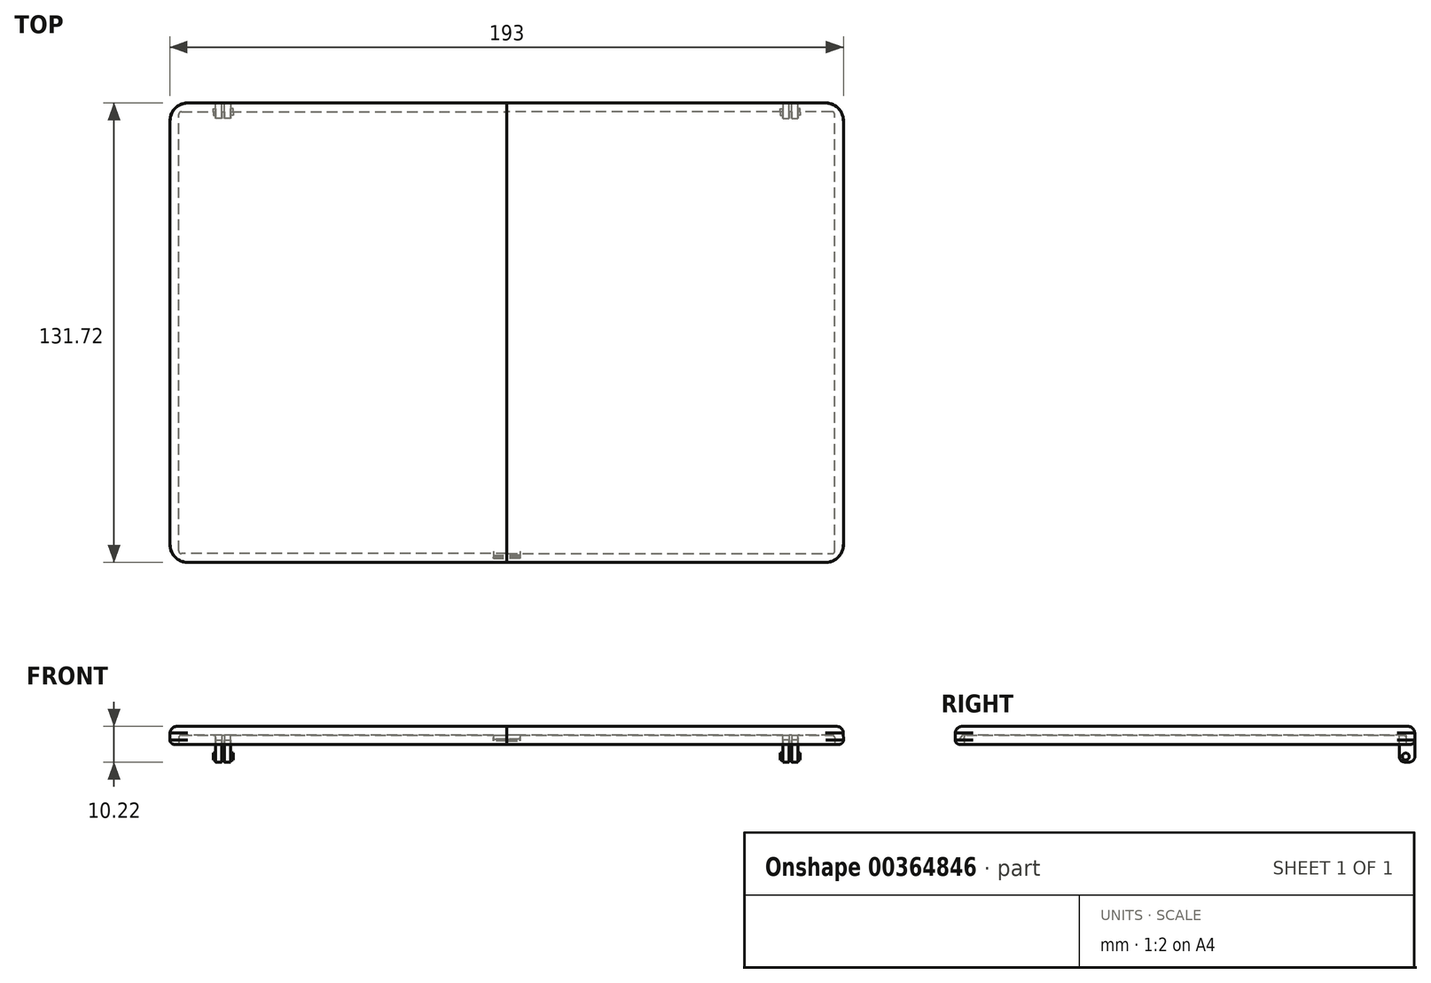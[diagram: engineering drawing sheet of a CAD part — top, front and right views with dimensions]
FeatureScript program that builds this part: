
annotation { "Feature Type Name" : "Feature", "Feature Type Description" : "" }
export const myFeature = defineFeature(function(context is Context, id is Id, definition is map)
    precondition{}
    {
        {
            var Q0;
            Q0=qCreatedBy(makeId("Top.planeOp"),FACE);
            var sketch = newSketch(context, id + "F0", { "sketchPlane" : qUnion([Q0])});
            skLineSegment(sketch, "E0.bottom", {"start": v(0, 65.88) * mm, "end": v(-96.52, 65.88) * mm});
            skLineSegment(sketch, "E0.top", {"start": v(0, -65.88) * mm, "end": v(-96.52, -65.88) * mm});
            skLineSegment(sketch, "E0.left", {"start": v(0, 65.88) * mm, "end": v(0, -65.88) * mm});
            skLineSegment(sketch, "E0.right", {"start": v(-96.52, 65.88) * mm, "end": v(-96.52, -65.88) * mm});
            skPoint(sketch, "E1", {"position": v(-96.52, 0) * mm});
            skLineSegment(sketch, "E2.bottom", {"start": v(0, 65.88) * mm, "end": v(96.52, 65.88) * mm});
            skLineSegment(sketch, "E2.top", {"start": v(0, -65.88) * mm, "end": v(96.52, -65.88) * mm});
            skLineSegment(sketch, "E2.right", {"start": v(96.52, 65.88) * mm, "end": v(96.52, -65.88) * mm});
            skSolve(sketch);
        }
        {
            var Q0;
            Q0=makeQuery(id+"F0.imprint","IMPRINT",FACE,{"disambiguationData":[TD([[makeQuery(id+"F0.imprint","IMPRINT",EDGE,{"derivedFrom":sQuery(id+"F0.wireOp",EDGE,"E0.bottom")}),1.0]])]});
            var Q1;
            Q1=makeQuery(id+"F0.imprint","IMPRINT",FACE,{"disambiguationData":[TD([[makeQuery(id+"F0.imprint","IMPRINT",EDGE,{"derivedFrom":sQuery(id+"F0.wireOp",EDGE,"E2.bottom")}),-1.0]])]});
            extrude(context, id + "F1", {"entities" : qUnion([Q0, Q1]), "depth" : 5.14 * mm, "hasDraft" : true, "draftAngle" : 1 * degree, "draftPullDirection" : true});
        }
        {
            var Q0;
            Q0=qCreatedBy(makeId("Top.planeOp"),FACE);
            var sketch = newSketch(context, id + "F2", { "sketchPlane" : qUnion([Q0])});
            skLineSegment(sketch, "E3.bottom", {"start": v(0, 72.75) * mm, "end": v(105.16, 72.75) * mm});
            skLineSegment(sketch, "E3.top", {"start": v(0, -72.07) * mm, "end": v(105.16, -72.07) * mm});
            skLineSegment(sketch, "E3.left", {"start": v(0, 72.75) * mm, "end": v(0, -72.07) * mm});
            skLineSegment(sketch, "E3.right", {"start": v(105.16, 72.75) * mm, "end": v(105.16, -72.07) * mm});
            skSolve(sketch);
        }
        {
            var Q0;
            Q0 = qSketchRegion(id + "F2", true);
            extrude(context, id + "F3", {"entities" : qUnion([Q0]), "operationType" : NewBodyOperationType.REMOVE, "depth" : 19.8 * mm});
        }
        {
            var Q0;
            Q0=makeQuery(id+"F1.opExtrude","SWEPT_EDGE",EDGE,{"disambiguationData":[OSD([sQuery(id+"F0.wireOp",EDGE,"E0.top"),sQuery(id+"F0.wireOp",EDGE,"E0.right")])]});
            var Q1;
            Q1=makeQuery(id+"F1.opExtrude","SWEPT_EDGE",EDGE,{"disambiguationData":[OSD([sQuery(id+"F0.wireOp",EDGE,"E0.bottom"),sQuery(id+"F0.wireOp",EDGE,"E0.right")])]});
            fillet(context, id + "F4", {"entities" : qUnion([Q0, Q1]), "radius" : 5.08 * mm, "tangentPropagation" : true, "allowEdgeOverflow" : false});
        }
        {
            var Q0;
            Q0=makeQuery(id+"F1.opExtrude","CAP_EDGE",EDGE,{"disambiguationData":[OSD([sQuery(id+"F0.wireOp",EDGE,"E0.top")])],"isStart":false});
            var Q1;
            {var subQ0=sQuery(id+"F0.wireOp",EDGE,"E0.right");var subQ1=sQuery(id+"F0.wireOp",EDGE,"E0.top");Q1=makeQuery(id+"F4.opFillet","BLEND_EDGE",EDGE,{"blendedFrom":[makeQuery(id+"F1.opExtrude","SWEPT_EDGE",EDGE,{"disambiguationData":[OSD([subQ1,subQ0])]}),makeQuery(id+"F1.opExtrude","CAP_FACE",FACE,{"disambiguationData":[OSD([sQuery(id+"F0.wireOp",EDGE,"E0.bottom"),subQ1,sQuery(id+"F0.wireOp",EDGE,"E0.left"),subQ0])],"isStart":false})],"blendedInto":[makeQuery(id+"F1.opExtrude","CAP_FACE",FACE,{"disambiguationData":[OSD([sQuery(id+"F0.wireOp",EDGE,"E0.bottom"),subQ1,sQuery(id+"F0.wireOp",EDGE,"E0.left"),subQ0])],"isStart":false})]});}
            var Q2;
            Q2=makeQuery(id+"F1.opExtrude","CAP_EDGE",EDGE,{"disambiguationData":[OSD([sQuery(id+"F0.wireOp",EDGE,"E0.right")])],"isStart":false});
            var Q3;
            {var subQ0=sQuery(id+"F0.wireOp",EDGE,"E0.right");var subQ1=sQuery(id+"F0.wireOp",EDGE,"E0.bottom");Q3=makeQuery(id+"F4.opFillet","BLEND_EDGE",EDGE,{"blendedFrom":[makeQuery(id+"F1.opExtrude","SWEPT_EDGE",EDGE,{"disambiguationData":[OSD([subQ1,subQ0])]}),makeQuery(id+"F1.opExtrude","CAP_FACE",FACE,{"disambiguationData":[OSD([subQ1,sQuery(id+"F0.wireOp",EDGE,"E0.top"),sQuery(id+"F0.wireOp",EDGE,"E0.left"),subQ0])],"isStart":false})],"blendedInto":[makeQuery(id+"F1.opExtrude","CAP_FACE",FACE,{"disambiguationData":[OSD([subQ1,sQuery(id+"F0.wireOp",EDGE,"E0.top"),sQuery(id+"F0.wireOp",EDGE,"E0.left"),subQ0])],"isStart":false})]});}
            var Q4;
            Q4=makeQuery(id+"F1.opExtrude","CAP_EDGE",EDGE,{"disambiguationData":[OSD([sQuery(id+"F0.wireOp",EDGE,"E0.bottom")])],"isStart":false});
            fillet(context, id + "F5", {"entities" : qUnion([Q0, Q1, Q2, Q3, Q4]), "radius" : 1.9 * mm, "tangentPropagation" : true, "allowEdgeOverflow" : false});
        }
        {
            var Q0;
            Q0=makeQuery(id+"F1.opExtrude","CAP_EDGE",EDGE,{"disambiguationData":[OSD([sQuery(id+"F0.wireOp",EDGE,"E0.right")])],"isStart":true});
            fillet(context, id + "F6", {"entities" : qUnion([Q0]), "radius" : 1.27 * mm, "tangentPropagation" : true, "allowEdgeOverflow" : false});
        }
        {
            var Q0;
            Q0=qCreatedBy(makeId("Top.planeOp"),FACE);
            var sketch = newSketch(context, id + "F7", { "sketchPlane" : qUnion([Q0])});
            skLineSegment(sketch, "E4.bottom", {"start": v(0, -63.34) * mm, "end": v(-93.22, -63.34) * mm});
            skLineSegment(sketch, "E4.left", {"start": v(0, -63.34) * mm, "end": v(0, 63.34) * mm});
            skLineSegment(sketch, "E4.right", {"start": v(-93.98, -62.58) * mm, "end": v(-93.98, 62.58) * mm});
            skPoint(sketch, "E5.visualSharp", {"position": v(-93.98, -63.34) * mm});
            skArc(sketch, "E5.filletArc", {"start": v(-93.22, -63.34) * mm, "mid": v(-93.76, -63.12) * mm, "end": v(-93.98, -62.58) * mm});
            skLineSegment(sketch, "E6", {"start": v(-93.22, 63.34) * mm, "end": v(0, 63.34) * mm});
            skPoint(sketch, "E7.visualSharp", {"position": v(-93.98, 63.34) * mm});
            skArc(sketch, "E7.filletArc", {"start": v(-93.22, 63.34) * mm, "mid": v(-93.76, 63.12) * mm, "end": v(-93.98, 62.58) * mm});
            skLineSegment(sketch, "E8.bottom", {"start": v(0, 63.34) * mm, "end": v(5.47, 63.34) * mm});
            skLineSegment(sketch, "E8.top", {"start": v(0, -63.34) * mm, "end": v(5.47, -63.34) * mm});
            skLineSegment(sketch, "E8.left", {"start": v(0, 63.34) * mm, "end": v(0, -63.34) * mm});
            skLineSegment(sketch, "E8.right", {"start": v(5.47, 63.34) * mm, "end": v(5.47, -63.34) * mm});
            skSolve(sketch);
        }
        {
            var Q0;
            Q0=makeQuery(id+"F7.imprint","IMPRINT",FACE,{"disambiguationData":[TD([[makeQuery(id+"F7.imprint","IMPRINT",EDGE,{"derivedFrom":sQuery(id+"F7.wireOp",EDGE,"E4.bottom")}),1.0]])]});
            var Q1;
            Q1=makeQuery(id+"F7.imprint","IMPRINT",FACE,{"disambiguationData":[TD([[makeQuery(id+"F7.imprint","IMPRINT",EDGE,{"derivedFrom":sQuery(id+"F7.wireOp",EDGE,"E4.bottom")}),-1.0]])]});
            var Q2;
            Q2=makeQuery(id+"F7.imprint","IMPRINT",FACE,{"disambiguationData":[TD([[makeQuery(id+"F7.imprint","IMPRINT",EDGE,{"derivedFrom":sQuery(id+"F7.wireOp",EDGE,"E8.bottom")}),-1.0]])]});
            extrude(context, id + "F8", {"entities" : qUnion([Q0, Q1, Q2]), "operationType" : NewBodyOperationType.REMOVE, "depth" : 2.6 * mm, "hasDraft" : true, "draftAngle" : 1 * degree, "draftPullDirection" : true});
        }
        {
            var Q0;
            Q0=qCreatedBy(makeId("Top.planeOp"),FACE);
            var sketch = newSketch(context, id + "F9", { "sketchPlane" : qUnion([Q0])});
            skLineSegment(sketch, "E9.bottom", {"start": v(-83.44, 65.86) * mm, "end": v(-81.66, 65.86) * mm});
            skLineSegment(sketch, "E9.top", {"start": v(-83.44, 61.41) * mm, "end": v(-81.66, 61.41) * mm});
            skLineSegment(sketch, "E9.left", {"start": v(-83.44, 61.41) * mm, "end": v(-83.44, 65.86) * mm});
            skLineSegment(sketch, "E9.right", {"start": v(-81.66, 61.41) * mm, "end": v(-81.66, 65.86) * mm});
            skLineSegment(sketch, "E10.top", {"start": v(-80.9, 61.41) * mm, "end": v(-79.12, 61.41) * mm});
            skLineSegment(sketch, "E10.left", {"start": v(-80.9, 61.41) * mm, "end": v(-80.9, 65.86) * mm});
            skLineSegment(sketch, "E10.right", {"start": v(-79.12, 65.86) * mm, "end": v(-79.12, 61.41) * mm});
            skLineSegment(sketch, "E11", {"start": v(-83.44, 63.64) * mm, "end": v(-79.12, 63.64) * mm, "construction": true});
            skPoint(sketch, "E12", {"position": v(-81.28, 63.64) * mm});
            skLineSegment(sketch, "E13", {"start": v(-80.9, 65.86) * mm, "end": v(-79.12, 65.86) * mm});
            skPoint(sketch, "E14.orphan", {"position": v(-79.12, 65.86) * mm});
            skSolve(sketch);
        }
        {
            var Q0;
            Q0=makeQuery(id+"F9.imprint","IMPRINT",FACE,{"disambiguationData":[TD([[makeQuery(id+"F9.imprint","IMPRINT",EDGE,{"derivedFrom":sQuery(id+"F9.wireOp",EDGE,"E9.bottom")}),-1.0]])]});
            var Q1;
            Q1=makeQuery(id+"F9.imprint","IMPRINT",FACE,{"disambiguationData":[TD([[makeQuery(id+"F9.imprint","IMPRINT",EDGE,{"derivedFrom":sQuery(id+"F9.wireOp",EDGE,"E10.top")}),1.0]])]});
            extrude(context, id + "F10", {"entities" : qUnion([Q0, Q1]), "operationType" : NewBodyOperationType.ADD, "oppositeDirection" : true, "depth" : 5.08 * mm, "hasSecondDirection" : true, "secondDirectionOppositeDirection" : false, "secondDirectionDepth" : 1.35 * mm});
        }
        {
            var Q0;
            Q0=makeQuery(id+"F10.opExtrude","CAP_FACE",FACE,{"disambiguationData":[OSD([sQuery(id+"F9.wireOp",EDGE,"E9.bottom"),sQuery(id+"F9.wireOp",EDGE,"E9.top"),sQuery(id+"F9.wireOp",EDGE,"E9.left"),sQuery(id+"F9.wireOp",EDGE,"E9.right")])],"isStart":true});
            var Q1;
            Q1=makeQuery(id+"F10.opExtrude","CAP_FACE",FACE,{"disambiguationData":[OSD([sQuery(id+"F9.wireOp",EDGE,"E10.top"),sQuery(id+"F9.wireOp",EDGE,"E10.left"),sQuery(id+"F9.wireOp",EDGE,"E10.right"),sQuery(id+"F9.wireOp",EDGE,"E13")])],"isStart":true});
            extrude(context, id + "F11", {"entities" : qUnion([Q0, Q1]), "operationType" : NewBodyOperationType.ADD, "depth" : 1.45 * mm});
        }
        {
            var Q0;
            Q0=qCreatedBy(makeId("Right.planeOp"),FACE);
            var sketch = newSketch(context, id + "F12", { "sketchPlane" : qUnion([Q0])});
            skLineSegment(sketch, "E15.bottom", {"start": v(-63.2, 2.6) * mm, "end": v(-64.66, 2.6) * mm});
            skLineSegment(sketch, "E15.top", {"start": v(-63.2, 0.93) * mm, "end": v(-64.66, 0.93) * mm});
            skLineSegment(sketch, "E15.left", {"start": v(-63.2, 2.6) * mm, "end": v(-63.2, 0.93) * mm});
            skLineSegment(sketch, "E15.right", {"start": v(-64.66, 2.6) * mm, "end": v(-64.66, 0.93) * mm});
            skLineSegment(sketch, "E16", {"start": v(-63.8, 2.6) * mm, "end": v(-64.66, 1.55) * mm});
            skLineSegment(sketch, "E17.bottom", {"start": v(-63.2, 0.93) * mm, "end": v(-63.64, 0.93) * mm});
            skLineSegment(sketch, "E17.top", {"start": v(-63.2, 0) * mm, "end": v(-63.64, 0) * mm});
            skLineSegment(sketch, "E17.left", {"start": v(-63.2, 0.93) * mm, "end": v(-63.2, 0) * mm});
            skLineSegment(sketch, "E17.right", {"start": v(-63.64, 0.93) * mm, "end": v(-63.64, 0) * mm});
            skSolve(sketch);
        }
        {
            var Q0;
            {var subQ1=sQuery(id+"F12.wireOp",EDGE,"E15.top");Q0=makeQuery(id+"F12.imprint","IMPRINT",FACE,{"disambiguationData":[TD([[makeQuery(id+"F12.imprint","IMPRINT",EDGE,{"derivedFrom":subQ1}),-1.0]])]});}
            var Q1;
            Q1=makeQuery(id+"F12.imprint","IMPRINT",FACE,{"disambiguationData":[TD([[makeQuery(id+"F12.imprint","IMPRINT",EDGE,{"derivedFrom":sQuery(id+"F12.wireOp",EDGE,"E17.bottom")}),1.0]])]});
            extrude(context, id + "F13", {"entities" : qUnion([Q0, Q1]), "operationType" : NewBodyOperationType.REMOVE, "oppositeDirection" : true, "depth" : 3.8 * mm});
        }
        {
            var Q0;
            Q0=makeQuery(id+"F10.opExtrude","CAP_EDGE",EDGE,{"disambiguationData":[OSD([sQuery(id+"F9.wireOp",EDGE,"E9.bottom")])],"isStart":false});
            var Q1;
            Q1=makeQuery(id+"F10.opExtrude","CAP_EDGE",EDGE,{"disambiguationData":[OSD([sQuery(id+"F9.wireOp",EDGE,"E13")])],"isStart":false});
            var Q2;
            Q2=makeQuery(id+"F10.opExtrude","CAP_EDGE",EDGE,{"disambiguationData":[OSD([sQuery(id+"F9.wireOp",EDGE,"E10.top")])],"isStart":false});
            var Q3;
            Q3=makeQuery(id+"F10.opExtrude","CAP_EDGE",EDGE,{"disambiguationData":[OSD([sQuery(id+"F9.wireOp",EDGE,"E9.top")])],"isStart":false});
            fillet(context, id + "F14", {"entities" : qUnion([Q0, Q1, Q2, Q3]), "radius" : 1.59 * mm, "tangentPropagation" : true, "allowEdgeOverflow" : false});
        }
        {
            var Q0;
            {var subQ0=sQuery(id+"F9.wireOp",EDGE,"E9.left");Q0=makeQuery(id+"FubJW8Bf5jqRAiZ_1.boolean.opBoolean","MERGE",FACE,{"derivedFrom":[makeQuery(id+"F10.opExtrude","SWEPT_FACE",FACE,{"disambiguationData":[OSD([subQ0])]}),makeQuery(id+"FubJW8Bf5jqRAiZ_1.opExtrude","SWEPT_FACE",FACE,{"disambiguationData":[OSD([subQ0])]})]});}
            var sketch = newSketch(context, id + "F15", { "sketchPlane" : qUnion([Q0])});
            skCircle(sketch, "E18", {"center": v(-63.26, -3.5) * mm, "radius": 1 * mm});
            skSolve(sketch);
        }
        {
            var Q0;
            Q0 = qSketchRegion(id + "F15", true);
            extrude(context, id + "F16", {"entities" : qUnion([Q0]), "operationType" : NewBodyOperationType.ADD, "depth" : 0.66 * mm});
        }
        {
            var Q0;
            {var subQ0=sQuery(id+"F9.wireOp",EDGE,"E10.right");Q0=makeQuery(id+"FubJW8Bf5jqRAiZ_1.boolean.opBoolean","MERGE",FACE,{"derivedFrom":[makeQuery(id+"F10.opExtrude","SWEPT_FACE",FACE,{"disambiguationData":[OSD([subQ0])]}),makeQuery(id+"FubJW8Bf5jqRAiZ_1.opExtrude","SWEPT_FACE",FACE,{"disambiguationData":[OSD([subQ0])]})]});}
            var sketch = newSketch(context, id + "F17", { "sketchPlane" : qUnion([Q0])});
            skCircle(sketch, "E19", {"center": v(63.26, -3.5) * mm, "radius": 1 * mm});
            skSolve(sketch);
        }
        {
            var Q0;
            Q0=makeQuery(id+"F17.imprint","IMPRINT",FACE,{"disambiguationData":[TD([[makeQuery(id+"F17.imprint","IMPRINT",EDGE,{"derivedFrom":sQuery(id+"F17.wireOp",EDGE,"E19")}),1.0]])]});
            extrude(context, id + "F18", {"entities" : qUnion([Q0]), "operationType" : NewBodyOperationType.ADD, "depth" : 0.76 * mm});
        }
        {
            var Q0;
            Q0=makeQuery(id+"F13.boolean.opBoolean","COPY",EDGE,{"derivedFrom":makeQuery(id+"F13.opExtrude","SWEPT_EDGE",EDGE,{"disambiguationData":[OSD([sQuery(id+"F12.wireOp",EDGE,"E15.top"),sQuery(id+"F12.wireOp",EDGE,"E17.bottom"),sQuery(id+"F12.wireOp",EDGE,"E17.right")])]})});
            chamfer(context, id + "F19", {"entities" : qUnion([Q0]), "chamferType" : ChamferType.OFFSET_ANGLE, "width" : 0.5 * mm, "oppositeDirection" : true, "angle" : 30 * degree, "tangentPropagation" : true});
        }
        {
            var Q0;
            Q0=makeQuery(id+"F8.boolean.opBoolean","COPY",EDGE,{"derivedFrom":makeQuery(id+"F8.opExtrude","CAP_EDGE",EDGE,{"disambiguationData":[OSD([sQuery(id+"F7.wireOp",EDGE,"E4.bottom")])],"isStart":false})});
            fillet(context, id + "F20", {"entities" : qUnion([Q0]), "radius" : 0.64 * mm, "tangentPropagation" : true, "allowEdgeOverflow" : false});
        }
        {
            var Q0;
            {var subQ0=sQuery(id+"F0.wireOp",EDGE,"E2.right");var subQ1=sQuery(id+"F0.wireOp",EDGE,"E2.top");var subQ2=sQuery(id+"F0.wireOp",EDGE,"E2.bottom");var subQ3=sQuery(id+"F0.wireOp",EDGE,"E0.right");var subQ4=sQuery(id+"F0.wireOp",EDGE,"E0.top");var subQ5=sQuery(id+"F0.wireOp",EDGE,"E0.bottom");Q0=makeQuery(id+"F5.opFillet","BLEND_FACE",FACE,{"disambiguationData":[OSD([subQ5,subQ4,subQ3,subQ2,subQ1,subQ0]),TDD([makeQuery(id+"F4.opFillet","BLEND_EDGE",EDGE,{"blendedFrom":[makeQuery(id+"F1.opExtrude","SWEPT_EDGE",EDGE,{"disambiguationData":[OSD([subQ4,subQ3])]}),makeQuery(id+"F1.opExtrude","CAP_FACE",FACE,{"disambiguationData":[OSD([subQ5,subQ4,subQ3,subQ2,subQ1,subQ0])],"isStart":false})],"blendedInto":[makeQuery(id+"F1.opExtrude","CAP_FACE",FACE,{"disambiguationData":[OSD([subQ5,subQ4,subQ3,subQ2,subQ1,subQ0])],"isStart":false})]})])]});}
            var Q1;
            Q1=makeQuery(id+"F5.opFillet","BLEND_FACE",FACE,{"disambiguationData":[OSD([sQuery(id+"F0.wireOp",EDGE,"E0.right")])]});
            var Q2;
            Q2=makeQuery(id+"F5.opFillet","BLEND_FACE",FACE,{"disambiguationData":[OSD([sQuery(id+"F0.wireOp",EDGE,"E0.bottom"),sQuery(id+"F0.wireOp",EDGE,"E2.bottom")])]});
            var Q3;
            Q3=makeQuery(id+"F5.opFillet","BLEND_FACE",FACE,{"disambiguationData":[OSD([sQuery(id+"F0.wireOp",EDGE,"E0.top"),sQuery(id+"F0.wireOp",EDGE,"E2.top")])]});
            var Q4;
            Q4=makeQuery(id+"F1.opExtrude","CAP_FACE",FACE,{"disambiguationData":[OSD([sQuery(id+"F0.wireOp",EDGE,"E0.bottom"),sQuery(id+"F0.wireOp",EDGE,"E0.top"),sQuery(id+"F0.wireOp",EDGE,"E0.right"),sQuery(id+"F0.wireOp",EDGE,"E2.bottom"),sQuery(id+"F0.wireOp",EDGE,"E2.top"),sQuery(id+"F0.wireOp",EDGE,"E2.right")])],"isStart":false});
            var Q5;
            Q5=makeQuery(id+"F6.opFillet","BLEND_FACE",FACE,{"disambiguationData":[OSD([sQuery(id+"F0.wireOp",EDGE,"E0.top"),sQuery(id+"F0.wireOp",EDGE,"E2.top")])]});
            var Q6;
            Q6=makeQuery(id+"F1.opExtrude","SWEPT_FACE",FACE,{"disambiguationData":[OSD([sQuery(id+"F0.wireOp",EDGE,"E0.top"),sQuery(id+"F0.wireOp",EDGE,"E2.top")])]});
            var Q7;
            {var subQ0=sQuery(id+"F7.wireOp",EDGE,"E8.bottom");var subQ1=sQuery(id+"F7.wireOp",EDGE,"E6");Q7=makeQuery(id+"F11.boolean.opBoolean","SPLIT",FACE,{"disambiguationData":[TD([makeQuery(id+"F3.boolean.opBoolean","COPY",FACE,{"derivedFrom":makeQuery(id+"F3.opExtrude","SWEPT_FACE",FACE,{"disambiguationData":[OSD([sQuery(id+"F2.wireOp",EDGE,"E3.left")])]})})])],"derivedFrom":makeQuery(id+"F8.boolean.opBoolean","COPY",FACE,{"derivedFrom":makeQuery(id+"F8.opExtrude","SWEPT_FACE",FACE,{"disambiguationData":[OSD([subQ1,subQ0])]})})});}
            var Q8;
            Q8=makeQuery(id+"F13.boolean.opBoolean","MERGE",FACE,{"derivedFrom":[makeQuery(id+"F8.boolean.opBoolean","COPY",FACE,{"derivedFrom":makeQuery(id+"F8.opExtrude","CAP_FACE",FACE,{"disambiguationData":[OSD([sQuery(id+"F7.wireOp",EDGE,"E4.bottom"),sQuery(id+"F7.wireOp",EDGE,"E4.right"),sQuery(id+"F7.wireOp",EDGE,"E5.filletArc"),sQuery(id+"F7.wireOp",EDGE,"E6"),sQuery(id+"F7.wireOp",EDGE,"E7.filletArc"),sQuery(id+"F7.wireOp",EDGE,"E8.bottom"),sQuery(id+"F7.wireOp",EDGE,"E8.top"),sQuery(id+"F7.wireOp",EDGE,"E8.right")])],"isStart":false})}),makeQuery(id+"F13.opExtrude","SWEPT_FACE",FACE,{"disambiguationData":[OSD([sQuery(id+"F12.wireOp",EDGE,"E15.bottom")])]})]});
            var Q9;
            Q9=makeQuery(id+"F3.boolean.opBoolean","COPY",FACE,{"derivedFrom":makeQuery(id+"F3.opExtrude","SWEPT_FACE",FACE,{"disambiguationData":[OSD([sQuery(id+"F2.wireOp",EDGE,"E3.left")])]})});
            var Q10;
            Q10=makeQuery(id+"F20.opFillet","BLEND_FACE",FACE,{"disambiguationData":[OSD([sQuery(id+"F7.wireOp",EDGE,"E7.filletArc")])]});
            var Q11;
            {var subQ0=sQuery(id+"F0.wireOp",EDGE,"E2.right");var subQ1=sQuery(id+"F0.wireOp",EDGE,"E2.top");var subQ2=sQuery(id+"F0.wireOp",EDGE,"E2.bottom");var subQ3=sQuery(id+"F0.wireOp",EDGE,"E0.right");var subQ4=sQuery(id+"F0.wireOp",EDGE,"E0.top");var subQ5=sQuery(id+"F0.wireOp",EDGE,"E0.bottom");Q11=makeQuery(id+"F5.opFillet","BLEND_FACE",FACE,{"disambiguationData":[OSD([subQ5,subQ4,subQ3,subQ2,subQ1,subQ0]),TDD([makeQuery(id+"F4.opFillet","BLEND_EDGE",EDGE,{"blendedFrom":[makeQuery(id+"F1.opExtrude","SWEPT_EDGE",EDGE,{"disambiguationData":[OSD([subQ5,subQ3])]}),makeQuery(id+"F1.opExtrude","CAP_FACE",FACE,{"disambiguationData":[OSD([subQ5,subQ4,subQ3,subQ2,subQ1,subQ0])],"isStart":false})],"blendedInto":[makeQuery(id+"F1.opExtrude","CAP_FACE",FACE,{"disambiguationData":[OSD([subQ5,subQ4,subQ3,subQ2,subQ1,subQ0])],"isStart":false})]})])]});}
            var Q12;
            {var subQ0=sQuery(id+"F0.wireOp",EDGE,"E2.right");var subQ1=sQuery(id+"F0.wireOp",EDGE,"E2.top");var subQ2=sQuery(id+"F0.wireOp",EDGE,"E2.bottom");var subQ3=sQuery(id+"F0.wireOp",EDGE,"E0.right");var subQ4=sQuery(id+"F0.wireOp",EDGE,"E0.top");var subQ5=sQuery(id+"F0.wireOp",EDGE,"E0.bottom");Q12=makeQuery(id+"F6.opFillet","BLEND_FACE",FACE,{"disambiguationData":[OSD([subQ5,subQ4,subQ3,subQ2,subQ1,subQ0]),TDD([makeQuery(id+"F4.opFillet","BLEND_EDGE",EDGE,{"blendedFrom":[makeQuery(id+"F1.opExtrude","SWEPT_EDGE",EDGE,{"disambiguationData":[OSD([subQ4,subQ3])]}),makeQuery(id+"F1.opExtrude","CAP_FACE",FACE,{"disambiguationData":[OSD([subQ5,subQ4,subQ3,subQ2,subQ1,subQ0])],"isStart":true})],"blendedInto":[makeQuery(id+"F1.opExtrude","CAP_FACE",FACE,{"disambiguationData":[OSD([subQ5,subQ4,subQ3,subQ2,subQ1,subQ0])],"isStart":true})]})])]});}
            var Q13;
            Q13=makeQuery(id+"F1.opExtrude","SWEPT_FACE",FACE,{"disambiguationData":[OSD([sQuery(id+"F0.wireOp",EDGE,"E0.right")])]});
            var Q14;
            Q14=makeQuery(id+"F14.opFillet","BLEND_FACE",FACE,{"disambiguationData":[OSD([sQuery(id+"F9.wireOp",EDGE,"E10.top")])]});
            var Q15;
            Q15=makeQuery(id+"F20.opFillet","BLEND_FACE",FACE,{"disambiguationData":[OSD([sQuery(id+"F7.wireOp",EDGE,"E4.bottom"),sQuery(id+"F7.wireOp",EDGE,"E8.top")])]});
            var Q16;
            Q16=makeQuery(id+"F8.boolean.opBoolean","COPY",FACE,{"derivedFrom":makeQuery(id+"F8.opExtrude","SWEPT_FACE",FACE,{"disambiguationData":[OSD([sQuery(id+"F7.wireOp",EDGE,"E4.right")])]})});
            var Q17;
            Q17=makeQuery(id+"F1.opExtrude","SWEPT_FACE",FACE,{"disambiguationData":[OSD([sQuery(id+"F0.wireOp",EDGE,"E0.bottom"),sQuery(id+"F0.wireOp",EDGE,"E2.bottom")])]});
            var Q18;
            {var subQ0=sQuery(id+"F0.wireOp",EDGE,"E2.top");var subQ1=sQuery(id+"F0.wireOp",EDGE,"E0.top");var subQ2=sQuery(id+"F0.wireOp",EDGE,"E2.bottom");var subQ3=sQuery(id+"F0.wireOp",EDGE,"E0.bottom");var subQ4=sQuery(id+"F0.wireOp",EDGE,"E0.right");var subQ5=sQuery(id+"F0.wireOp",EDGE,"E2.right");var subQ6=makeQuery(id+"F1.opExtrude","CAP_FACE",FACE,{"disambiguationData":[OSD([subQ3,subQ1,subQ4,subQ2,subQ0,subQ5])],"isStart":true});Q18=makeQuery(id+"F10.boolean.opBoolean","SPLIT",FACE,{"disambiguationData":[TD([makeQuery(id+"F6.opFillet","BLEND_FACE",FACE,{"disambiguationData":[OSD([subQ4])]})])],"derivedFrom":subQ6});}
            var Q19;
            Q19=makeQuery(id+"F20.opFillet","BLEND_FACE",FACE,{"disambiguationData":[OSD([sQuery(id+"F7.wireOp",EDGE,"E4.right")])]});
            var Q20;
            {var subQ0=sQuery(id+"F9.wireOp",EDGE,"E10.top");Q20=makeQuery(id+"F11.boolean.opBoolean","MERGE",FACE,{"derivedFrom":[makeQuery(id+"F10.opExtrude","SWEPT_FACE",FACE,{"disambiguationData":[OSD([subQ0])]}),makeQuery(id+"F11.opExtrude","SWEPT_FACE",FACE,{"disambiguationData":[OSD([subQ0])]})]});}
            var Q21;
            Q21=makeQuery(id+"F18.opExtrude","SWEPT_FACE",FACE,{"disambiguationData":[OSD([sQuery(id+"F17.wireOp",EDGE,"E19")])]});
            var Q22;
            {var subQ0=sQuery(id+"F0.wireOp",EDGE,"E2.bottom");var subQ1=sQuery(id+"F0.wireOp",EDGE,"E0.bottom");Q22=makeQuery(id+"F10.boolean.opBoolean","SPLIT",FACE,{"disambiguationData":[TD([makeQuery(id+"F10.opExtrude","SWEPT_FACE",FACE,{"disambiguationData":[OSD([sQuery(id+"F9.wireOp",EDGE,"E10.right")])]})])],"derivedFrom":makeQuery(id+"F1.opExtrude","CAP_FACE",FACE,{"disambiguationData":[OSD([subQ1,sQuery(id+"F0.wireOp",EDGE,"E0.top"),sQuery(id+"F0.wireOp",EDGE,"E0.right"),subQ0,sQuery(id+"F0.wireOp",EDGE,"E2.top"),sQuery(id+"F0.wireOp",EDGE,"E2.right")])],"isStart":true})});}
            var Q23;
            {var subQ0=sQuery(id+"F9.wireOp",EDGE,"E10.right");Q23=makeQuery(id+"F11.boolean.opBoolean","MERGE",FACE,{"derivedFrom":[makeQuery(id+"F10.opExtrude","SWEPT_FACE",FACE,{"disambiguationData":[OSD([subQ0])]}),makeQuery(id+"F11.opExtrude","SWEPT_FACE",FACE,{"disambiguationData":[OSD([subQ0])]})]});}
            var Q24;
            Q24=makeQuery(id+"F6.opFillet","BLEND_FACE",FACE,{"disambiguationData":[OSD([sQuery(id+"F0.wireOp",EDGE,"E0.right")])]});
            var Q25;
            Q25=makeQuery(id+"F4.opFillet","BLEND_FACE",FACE,{"disambiguationData":[OSD([sQuery(id+"F0.wireOp",EDGE,"E0.top"),sQuery(id+"F0.wireOp",EDGE,"E0.right")])]});
            var Q26;
            Q26=makeQuery(id+"F20.opFillet","BLEND_FACE",FACE,{"disambiguationData":[OSD([sQuery(id+"F7.wireOp",EDGE,"E5.filletArc")])]});
            var Q27;
            Q27=makeQuery(id+"F8.boolean.opBoolean","COPY",FACE,{"derivedFrom":makeQuery(id+"F8.opExtrude","SWEPT_FACE",FACE,{"disambiguationData":[OSD([sQuery(id+"F7.wireOp",EDGE,"E4.bottom"),sQuery(id+"F7.wireOp",EDGE,"E8.top")])]})});
            var Q28;
            Q28=makeQuery(id+"F13.boolean.opBoolean","COPY",FACE,{"derivedFrom":makeQuery(id+"F13.opExtrude","SWEPT_FACE",FACE,{"disambiguationData":[OSD([sQuery(id+"F12.wireOp",EDGE,"E17.right")])]})});
            var Q29;
            Q29=makeQuery(id+"F6.opFillet","BLEND_FACE",FACE,{"disambiguationData":[OSD([sQuery(id+"F0.wireOp",EDGE,"E0.bottom"),sQuery(id+"F0.wireOp",EDGE,"E2.bottom")])]});
            var Q30;
            Q30=makeQuery(id+"F18.opExtrude","CAP_FACE",FACE,{"disambiguationData":[OSD([sQuery(id+"F17.wireOp",EDGE,"E19")])],"isStart":false});
            var Q31;
            Q31=makeQuery(id+"F20.opFillet","BLEND_FACE",FACE,{"disambiguationData":[OSD([sQuery(id+"F7.wireOp",EDGE,"E6"),sQuery(id+"F7.wireOp",EDGE,"E8.bottom")])]});
            var Q32;
            Q32=makeQuery(id+"F13.boolean.opBoolean","COPY",FACE,{"derivedFrom":makeQuery(id+"F13.opExtrude","SWEPT_FACE",FACE,{"disambiguationData":[OSD([sQuery(id+"F12.wireOp",EDGE,"E16")])]})});
            var Q33;
            Q33=makeQuery(id+"F10.opExtrude","SWEPT_FACE",FACE,{"disambiguationData":[OSD([sQuery(id+"F9.wireOp",EDGE,"E13")])]});
            var Q34;
            Q34=makeQuery(id+"F13.boolean.opBoolean","COPY",FACE,{"derivedFrom":makeQuery(id+"F13.opExtrude","SWEPT_FACE",FACE,{"disambiguationData":[OSD([sQuery(id+"F12.wireOp",EDGE,"E15.right")])]})});
            var Q35;
            Q35=makeQuery(id+"F19.opChamfer","BLEND_FACE",FACE,{"disambiguationData":[OSD([sQuery(id+"F12.wireOp",EDGE,"E15.top"),sQuery(id+"F12.wireOp",EDGE,"E17.bottom"),sQuery(id+"F12.wireOp",EDGE,"E17.right")])]});
            var Q36;
            {var subQ1=sQuery(id+"F7.wireOp",EDGE,"E8.bottom");var subQ2=sQuery(id+"F7.wireOp",EDGE,"E6");var subQ3=sQuery(id+"F9.wireOp",EDGE,"E9.right");Q36=makeQuery(id+"F11.boolean.opBoolean","SPLIT",FACE,{"disambiguationData":[TD([makeQuery(id+"F10.opExtrude","SWEPT_FACE",FACE,{"disambiguationData":[OSD([subQ3])]})])],"derivedFrom":makeQuery(id+"F8.boolean.opBoolean","COPY",FACE,{"derivedFrom":makeQuery(id+"F8.opExtrude","SWEPT_FACE",FACE,{"disambiguationData":[OSD([subQ2,subQ1])]})})});}
            var Q37;
            Q37=makeQuery(id+"F14.opFillet","BLEND_FACE",FACE,{"disambiguationData":[OSD([sQuery(id+"F9.wireOp",EDGE,"E13")])]});
            var Q38;
            Q38=makeQuery(id+"F10.opExtrude","CAP_FACE",FACE,{"disambiguationData":[OSD([sQuery(id+"F9.wireOp",EDGE,"E10.top"),sQuery(id+"F9.wireOp",EDGE,"E10.left"),sQuery(id+"F9.wireOp",EDGE,"E10.right"),sQuery(id+"F9.wireOp",EDGE,"E13")])],"isStart":false});
            var Q39;
            {var subQ0=sQuery(id+"F9.wireOp",EDGE,"E9.top");Q39=makeQuery(id+"F11.boolean.opBoolean","MERGE",FACE,{"derivedFrom":[makeQuery(id+"F10.opExtrude","SWEPT_FACE",FACE,{"disambiguationData":[OSD([subQ0])]}),makeQuery(id+"F11.opExtrude","SWEPT_FACE",FACE,{"disambiguationData":[OSD([subQ0])]})]});}
            var Q40;
            {var subQ0=sQuery(id+"F9.wireOp",EDGE,"E9.left");Q40=makeQuery(id+"F11.boolean.opBoolean","MERGE",FACE,{"derivedFrom":[makeQuery(id+"F10.opExtrude","SWEPT_FACE",FACE,{"disambiguationData":[OSD([subQ0])]}),makeQuery(id+"F11.opExtrude","SWEPT_FACE",FACE,{"disambiguationData":[OSD([subQ0])]})]});}
            var Q41;
            {var subQ0=sQuery(id+"F9.wireOp",EDGE,"E10.left");Q41=makeQuery(id+"F11.boolean.opBoolean","MERGE",FACE,{"derivedFrom":[makeQuery(id+"F10.opExtrude","SWEPT_FACE",FACE,{"disambiguationData":[OSD([subQ0])]}),makeQuery(id+"F11.opExtrude","SWEPT_FACE",FACE,{"disambiguationData":[OSD([subQ0])]})]});}
            var Q42;
            Q42=makeQuery(id+"F8.boolean.opBoolean","COPY",FACE,{"derivedFrom":makeQuery(id+"F8.opExtrude","SWEPT_FACE",FACE,{"disambiguationData":[OSD([sQuery(id+"F7.wireOp",EDGE,"E5.filletArc")])]})});
            var Q43;
            Q43=makeQuery(id+"F13.boolean.opBoolean","COPY",FACE,{"derivedFrom":makeQuery(id+"F13.opExtrude","CAP_FACE",FACE,{"disambiguationData":[OSD([sQuery(id+"F12.wireOp",EDGE,"E15.bottom"),sQuery(id+"F12.wireOp",EDGE,"E15.top"),sQuery(id+"F12.wireOp",EDGE,"E15.left"),sQuery(id+"F12.wireOp",EDGE,"E15.right"),sQuery(id+"F12.wireOp",EDGE,"E16"),sQuery(id+"F12.wireOp",EDGE,"E17.top"),sQuery(id+"F12.wireOp",EDGE,"E17.left"),sQuery(id+"F12.wireOp",EDGE,"E17.right")])],"isStart":false})});
            var Q44;
            {var subQ0=sQuery(id+"F9.wireOp",EDGE,"E9.right");Q44=makeQuery(id+"F11.boolean.opBoolean","MERGE",FACE,{"derivedFrom":[makeQuery(id+"F10.opExtrude","SWEPT_FACE",FACE,{"disambiguationData":[OSD([subQ0])]}),makeQuery(id+"F11.opExtrude","SWEPT_FACE",FACE,{"disambiguationData":[OSD([subQ0])]})]});}
            var Q45;
            {var subQ0=sQuery(id+"F0.wireOp",EDGE,"E2.bottom");var subQ1=sQuery(id+"F0.wireOp",EDGE,"E0.bottom");Q45=makeQuery(id+"F10.boolean.opBoolean","SPLIT",FACE,{"disambiguationData":[TD([makeQuery(id+"F10.opExtrude","SWEPT_FACE",FACE,{"disambiguationData":[OSD([sQuery(id+"F9.wireOp",EDGE,"E9.right")])]})])],"derivedFrom":makeQuery(id+"F1.opExtrude","CAP_FACE",FACE,{"disambiguationData":[OSD([subQ1,sQuery(id+"F0.wireOp",EDGE,"E0.top"),sQuery(id+"F0.wireOp",EDGE,"E0.right"),subQ0,sQuery(id+"F0.wireOp",EDGE,"E2.top"),sQuery(id+"F0.wireOp",EDGE,"E2.right")])],"isStart":true})});}
            var Q46;
            Q46=makeQuery(id+"F14.opFillet","BLEND_FACE",FACE,{"disambiguationData":[OSD([sQuery(id+"F9.wireOp",EDGE,"E9.top")])]});
            var Q47;
            {var subQ1=sQuery(id+"F7.wireOp",EDGE,"E7.filletArc");var subQ2=sQuery(id+"F7.wireOp",EDGE,"E8.bottom");var subQ3=sQuery(id+"F7.wireOp",EDGE,"E6");Q47=makeQuery(id+"F11.boolean.opBoolean","SPLIT",FACE,{"disambiguationData":[TD([makeQuery(id+"F8.boolean.opBoolean","COPY",FACE,{"derivedFrom":makeQuery(id+"F8.opExtrude","SWEPT_FACE",FACE,{"disambiguationData":[OSD([subQ1])]})})])],"derivedFrom":makeQuery(id+"F8.boolean.opBoolean","COPY",FACE,{"derivedFrom":makeQuery(id+"F8.opExtrude","SWEPT_FACE",FACE,{"disambiguationData":[OSD([subQ3,subQ2])]})})});}
            var Q48;
            {var subQ0=sQuery(id+"F0.wireOp",EDGE,"E2.right");var subQ1=sQuery(id+"F0.wireOp",EDGE,"E2.top");var subQ2=sQuery(id+"F0.wireOp",EDGE,"E2.bottom");var subQ3=sQuery(id+"F0.wireOp",EDGE,"E0.right");var subQ4=sQuery(id+"F0.wireOp",EDGE,"E0.top");var subQ5=sQuery(id+"F0.wireOp",EDGE,"E0.bottom");Q48=makeQuery(id+"F6.opFillet","BLEND_FACE",FACE,{"disambiguationData":[OSD([subQ5,subQ4,subQ3,subQ2,subQ1,subQ0]),TDD([makeQuery(id+"F4.opFillet","BLEND_EDGE",EDGE,{"blendedFrom":[makeQuery(id+"F1.opExtrude","SWEPT_EDGE",EDGE,{"disambiguationData":[OSD([subQ5,subQ3])]}),makeQuery(id+"F1.opExtrude","CAP_FACE",FACE,{"disambiguationData":[OSD([subQ5,subQ4,subQ3,subQ2,subQ1,subQ0])],"isStart":true})],"blendedInto":[makeQuery(id+"F1.opExtrude","CAP_FACE",FACE,{"disambiguationData":[OSD([subQ5,subQ4,subQ3,subQ2,subQ1,subQ0])],"isStart":true})]})])]});}
            var Q49;
            Q49=makeQuery(id+"F4.opFillet","BLEND_FACE",FACE,{"disambiguationData":[OSD([sQuery(id+"F0.wireOp",EDGE,"E0.bottom"),sQuery(id+"F0.wireOp",EDGE,"E0.right")])]});
            var Q50;
            Q50=makeQuery(id+"F16.opExtrude","SWEPT_FACE",FACE,{"disambiguationData":[OSD([sQuery(id+"F15.wireOp",EDGE,"E18")])]});
            var Q51;
            Q51=makeQuery(id+"F13.boolean.opBoolean","COPY",FACE,{"derivedFrom":makeQuery(id+"F13.opExtrude","SWEPT_FACE",FACE,{"disambiguationData":[OSD([sQuery(id+"F12.wireOp",EDGE,"E15.top")])]})});
            var Q52;
            Q52=makeQuery(id+"F8.boolean.opBoolean","COPY",FACE,{"derivedFrom":makeQuery(id+"F8.opExtrude","SWEPT_FACE",FACE,{"disambiguationData":[OSD([sQuery(id+"F7.wireOp",EDGE,"E7.filletArc")])]})});
            var Q53;
            Q53=makeQuery(id+"F10.opExtrude","SWEPT_FACE",FACE,{"disambiguationData":[OSD([sQuery(id+"F9.wireOp",EDGE,"E9.bottom")])]});
            var Q54;
            Q54=makeQuery(id+"F16.opExtrude","CAP_FACE",FACE,{"disambiguationData":[OSD([sQuery(id+"F15.wireOp",EDGE,"E18")])],"isStart":false});
            var Q55;
            Q55=makeQuery(id+"F14.opFillet","BLEND_FACE",FACE,{"disambiguationData":[OSD([sQuery(id+"F9.wireOp",EDGE,"E9.bottom")])]});
            var Q56;
            Q56=makeQuery(id+"F10.opExtrude","CAP_FACE",FACE,{"disambiguationData":[OSD([sQuery(id+"F9.wireOp",EDGE,"E9.bottom"),sQuery(id+"F9.wireOp",EDGE,"E9.top"),sQuery(id+"F9.wireOp",EDGE,"E9.left"),sQuery(id+"F9.wireOp",EDGE,"E9.right")])],"isStart":false});
            var Q57;
            Q57=qCreatedBy(makeId("Right.planeOp"),FACE);
            mirror(context, id + "F21", {"patternType" : MirrorType.FACE, "faces" : qUnion([Q0, Q1, Q2, Q3, Q4, Q5, Q6, Q7, Q8, Q9, Q10, Q11, Q12, Q13, Q14, Q15, Q16, Q17, Q18, Q19, Q20, Q21, Q22, Q23, Q24, Q25, Q26, Q27, Q28, Q29, Q30, Q31, Q32, Q33, Q34, Q35, Q36, Q37, Q38, Q39, Q40, Q41, Q42, Q43, Q44, Q45, Q46, Q47, Q48, Q49, Q50, Q51, Q52, Q53, Q54, Q55, Q56]), "mirrorPlane" : qUnion([Q57])});
        }
    });
